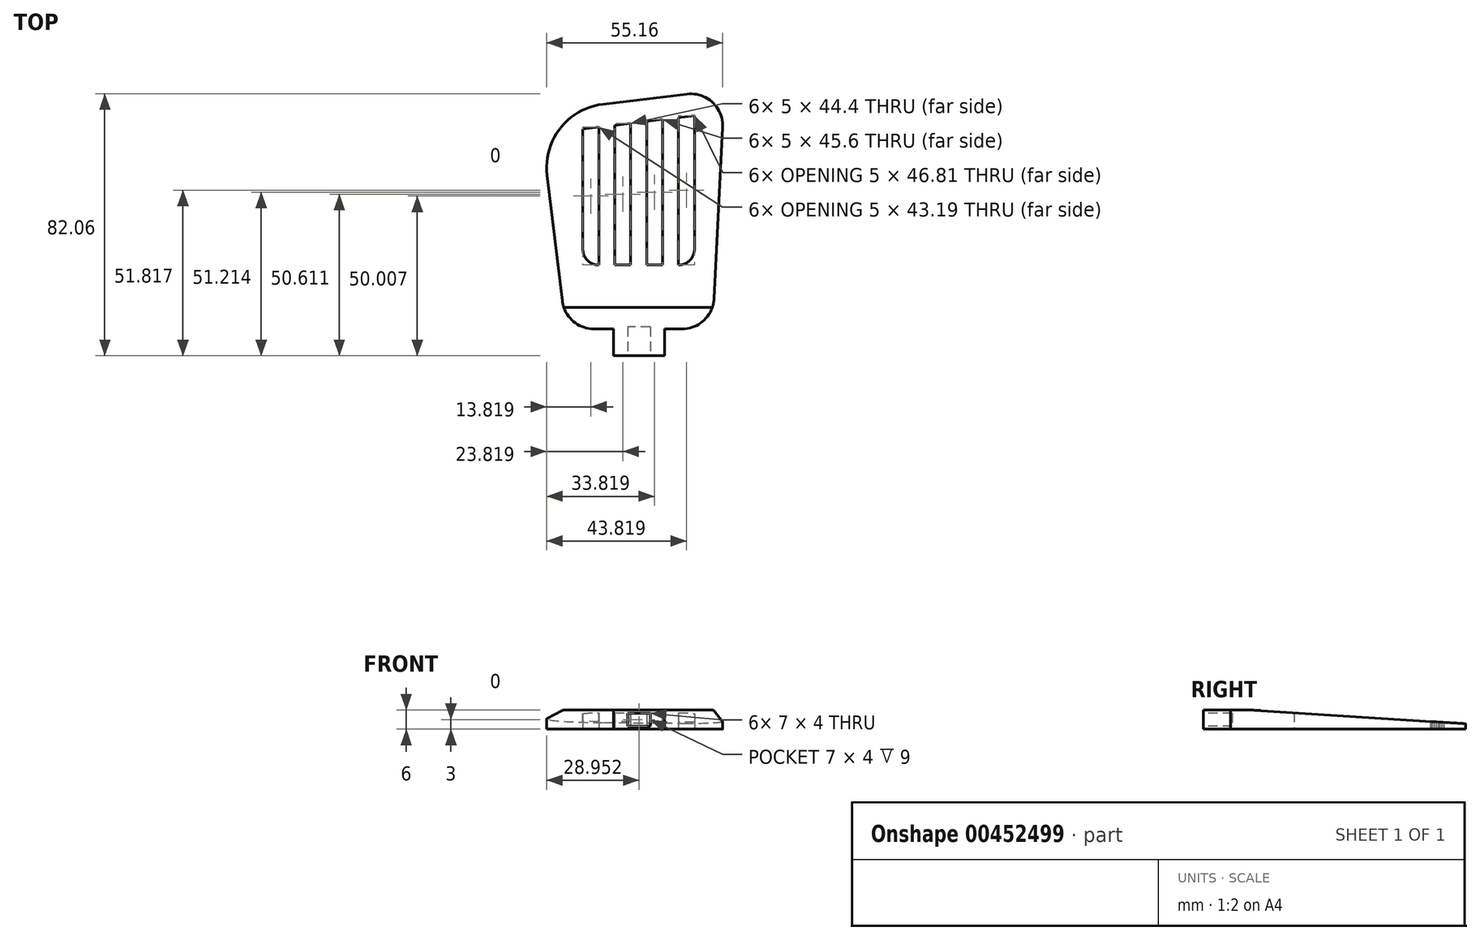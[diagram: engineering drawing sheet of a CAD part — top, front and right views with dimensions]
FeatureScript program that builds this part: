
annotation { "Feature Type Name" : "Feature", "Feature Type Description" : "" }
export const myFeature = defineFeature(function(context is Context, id is Id, definition is map)
    precondition{}
    {
        {
            var Q0;
            Q0=qCreatedBy(makeId("Top.planeOp"),FACE);
            var sketch = newSketch(context, id + "F0", { "sketchPlane" : qUnion([Q0])});
            skLineSegment(sketch, "E0", {"start": v(-1.99, 0) * mm, "end": v(14.01, 0) * mm});
            skLineSegment(sketch, "E1", {"start": v(14.01, 0) * mm, "end": v(14.01, 8.41) * mm});
            skLineSegment(sketch, "E2", {"start": v(14.01, 8.41) * mm, "end": v(19.5, 8.41) * mm});
            skLineSegment(sketch, "E3", {"start": v(29.5, 17.9) * mm, "end": v(32.2, 71.56) * mm});
            skLineSegment(sketch, "E4", {"start": v(21.02, 81.99) * mm, "end": v(-5.34, 78.8) * mm});
            skLineSegment(sketch, "E5", {"start": v(-22.8, 56.56) * mm, "end": v(-18.05, 17.21) * mm});
            skLineSegment(sketch, "E6", {"start": v(-8.12, 8.41) * mm, "end": v(-1.99, 8.41) * mm});
            skLineSegment(sketch, "E7", {"start": v(-1.99, 8.41) * mm, "end": v(-1.99, 0) * mm});
            skLineSegment(sketch, "E8", {"start": v(-6.62, 28.41) * mm, "end": v(-6.62, 28.41) * mm});
            skLineSegment(sketch, "E9", {"start": v(23.38, 33.41) * mm, "end": v(23.38, 75.22) * mm});
            skLineSegment(sketch, "E10", {"start": v(23.38, 75.22) * mm, "end": v(18.38, 74.62) * mm});
            skLineSegment(sketch, "E11", {"start": v(-11.62, 71) * mm, "end": v(-11.62, 33.41) * mm});
            skLineSegment(sketch, "E12", {"start": v(-6.62, 71.6) * mm, "end": v(-6.62, 28.41) * mm});
            skLineSegment(sketch, "E13", {"start": v(-1.62, 72.2) * mm, "end": v(-1.62, 28.41) * mm});
            skLineSegment(sketch, "E14", {"start": v(3.38, 72.8) * mm, "end": v(3.38, 28.41) * mm});
            skLineSegment(sketch, "E15", {"start": v(18.38, 28.41) * mm, "end": v(18.38, 74.62) * mm});
            skLineSegment(sketch, "E16", {"start": v(13.38, 74.02) * mm, "end": v(13.38, 28.41) * mm});
            skLineSegment(sketch, "E17", {"start": v(8.38, 28.41) * mm, "end": v(8.38, 73.41) * mm});
            skLineSegment(sketch, "E18.trimOffspring", {"start": v(-6.62, 71.6) * mm, "end": v(-11.62, 71) * mm});
            skLineSegment(sketch, "E19.trimOffspring", {"start": v(-1.62, 28.41) * mm, "end": v(3.38, 28.41) * mm});
            skLineSegment(sketch, "E20.trimOffspring", {"start": v(8.38, 28.41) * mm, "end": v(13.38, 28.41) * mm});
            skLineSegment(sketch, "E21.trimOffspring", {"start": v(3.38, 72.8) * mm, "end": v(-1.62, 72.2) * mm});
            skLineSegment(sketch, "E22.trimOffspring", {"start": v(13.38, 74.02) * mm, "end": v(8.38, 73.41) * mm});
            skLineSegment(sketch, "E23.trimOffspring", {"start": v(18.38, 28.41) * mm, "end": v(18.38, 28.41) * mm});
            skPoint(sketch, "E24.visualSharp", {"position": v(-25.2, 76.41) * mm});
            skArc(sketch, "E24.filletArc", {"start": v(-5.34, 78.8) * mm, "mid": v(-18.68, 71.3) * mm, "end": v(-22.8, 56.56) * mm});
            skPoint(sketch, "E25.visualSharp", {"position": v(32.8, 83.41) * mm});
            skArc(sketch, "E25.filletArc", {"start": v(32.2, 71.56) * mm, "mid": v(29.04, 79.37) * mm, "end": v(21.02, 81.99) * mm});
            skPoint(sketch, "E26.visualSharp", {"position": v(-16.99, 8.41) * mm});
            skArc(sketch, "E26.filletArc", {"start": v(-18.05, 17.21) * mm, "mid": v(-14.76, 10.93) * mm, "end": v(-8.12, 8.41) * mm});
            skPoint(sketch, "E27.visualSharp", {"position": v(29.01, 8.41) * mm});
            skArc(sketch, "E27.filletArc", {"start": v(19.5, 8.41) * mm, "mid": v(26.4, 11.16) * mm, "end": v(29.5, 17.9) * mm});
            skPoint(sketch, "E28.visualSharp", {"position": v(-11.62, 28.41) * mm});
            skArc(sketch, "E28.filletArc", {"start": v(-11.62, 33.41) * mm, "mid": v(-10.16, 29.88) * mm, "end": v(-6.62, 28.41) * mm});
            skPoint(sketch, "E29.visualSharp", {"position": v(23.38, 28.41) * mm});
            skArc(sketch, "E29.filletArc", {"start": v(18.38, 28.41) * mm, "mid": v(21.91, 29.88) * mm, "end": v(23.38, 33.41) * mm});
            skSolve(sketch);
        }
        {
            var Q0;
            Q0=makeQuery(id+"F0.imprint","IMPRINT",FACE,{"disambiguationData":[TD([[makeQuery(id+"F0.imprint","IMPRINT",EDGE,{"derivedFrom":sQuery(id+"F0.wireOp",EDGE,"E0")}),1.0]])]});
            extrude(context, id + "F1", {"entities" : qUnion([Q0]), "depth" : 6 * mm});
        }
        {
            var Q0;
            Q0=qCreatedBy(makeId("Right.planeOp"),FACE);
            var sketch = newSketch(context, id + "F2", { "sketchPlane" : qUnion([Q0])});
            skLineSegment(sketch, "E30", {"start": v(8.15, 6.44) * mm, "end": v(82.89, 1.67) * mm});
            skLineSegment(sketch, "E31", {"start": v(82.89, 1.67) * mm, "end": v(82.89, 7.08) * mm});
            skLineSegment(sketch, "E32", {"start": v(82.89, 7.08) * mm, "end": v(8.15, 6.44) * mm});
            skLineSegment(sketch, "E33", {"start": v(83.56, 0) * mm, "end": v(0, 0) * mm, "construction": true});
            skSolve(sketch);
        }
        {
            var Q0;
            Q0 = qSketchRegion(id + "F2", true);
            extrude(context, id + "F3", {"entities" : qUnion([Q0]), "operationType" : NewBodyOperationType.REMOVE, "endBound" : BoundingType.THROUGH_ALL, "depth" : 25 * mm, "hasSecondDirection" : true, "secondDirectionBound" : SecondDirectionBoundingType.THROUGH_ALL, "secondDirectionOppositeDirection" : true, "secondDirectionDepth" : 25 * mm});
        }
        {
            var Q0;
            Q0=makeQuery(id+"F1.opExtrude","SWEPT_FACE",FACE,{"disambiguationData":[OSD([sQuery(id+"F0.wireOp",EDGE,"E0")])]});
            var sketch = newSketch(context, id + "F4", { "sketchPlane" : qUnion([Q0])});
            skLineSegment(sketch, "E34.bottom", {"start": v(9.51, 5) * mm, "end": v(2.51, 5) * mm});
            skLineSegment(sketch, "E34.top", {"start": v(9.51, 1) * mm, "end": v(2.51, 1) * mm});
            skLineSegment(sketch, "E34.left", {"start": v(9.51, 5) * mm, "end": v(9.51, 1) * mm});
            skLineSegment(sketch, "E34.right", {"start": v(2.51, 5) * mm, "end": v(2.51, 1) * mm});
            skPoint(sketch, "E34.middle", {"position": v(6.01, 3) * mm});
            skSolve(sketch);
        }
        {
            var Q0;
            Q0=makeQuery(id+"F4.imprint","IMPRINT",FACE,{"disambiguationData":[TD([[makeQuery(id+"F4.imprint","IMPRINT",EDGE,{"derivedFrom":sQuery(id+"F4.wireOp",EDGE,"E34.bottom")}),1.0]])]});
            extrude(context, id + "F5", {"entities" : qUnion([Q0]), "operationType" : NewBodyOperationType.REMOVE, "oppositeDirection" : true, "depth" : 9 * mm});
        }
    });
